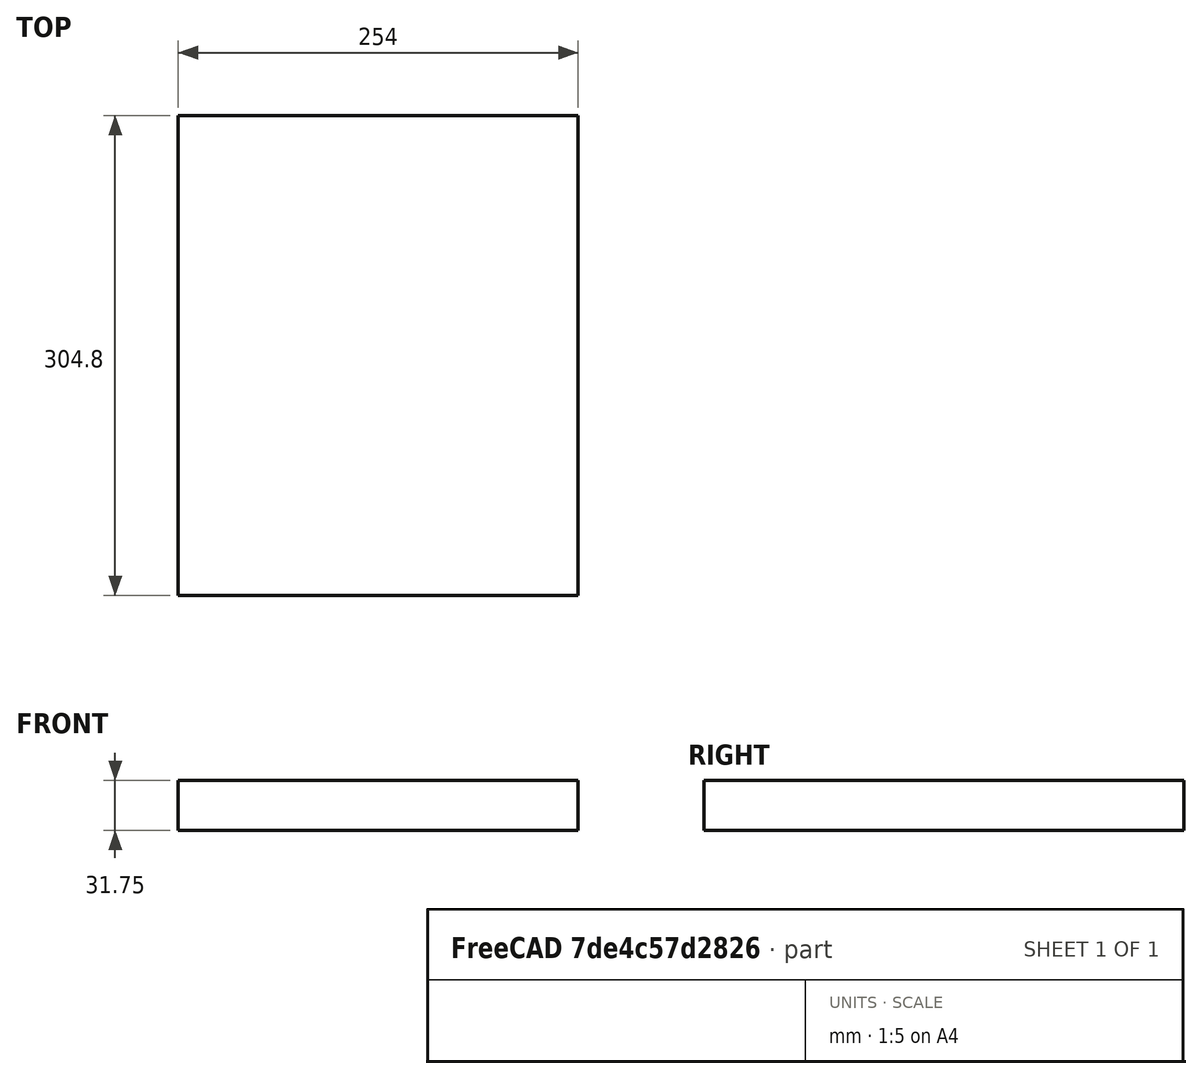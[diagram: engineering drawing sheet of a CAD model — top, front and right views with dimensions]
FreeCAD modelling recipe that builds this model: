
FCSTD DOCUMENT  (FreeCAD 0.16RUnknown)
Label: Base
License: All rights reserved
LicenseURL: http://en.wikipedia.org/wiki/All_rights_reserved
objects: Sketcher::SketchObject×1, Part::Box×1
note: 2 computed .brp shape members not serialized (recipe doc carries the construction recipe); baked Part::Feature solids carry a one-line shape summary decoded from their .brp

FEATURE [Sketcher::SketchObject] Sketch
  sketch-geometry (4):
    g0: LineSegment StartX=0 StartY=0 StartZ=0 EndX=304.8 EndY=0 EndZ=0
    g1: LineSegment StartX=304.8 StartY=0 StartZ=0 EndX=304.8 EndY=254 EndZ=0
    g2: LineSegment StartX=304.8 StartY=254 StartZ=0 EndX=0 EndY=254 EndZ=0
    g3: LineSegment StartX=0 StartY=254 StartZ=0 EndX=0 EndY=0 EndZ=0
  constraints (11):
    c: Coincident(g0,g1)
    c: Coincident(g1,g2)
    c: Coincident(g2,g3)
    c: Coincident(g3,g0)
    c: Horizontal(g0)
    c: Horizontal(g2)
    c: Vertical(g1)
    c: Vertical(g3)
    c: Coincident(g0,g-1)
    c: DistanceX(g0,g0) = 304.8
    c: DistanceY(g3,g3) = 254
FEATURE [Part::Box] Box  label="Cube"
  Height = 31.75
  Length = 254
  Width = 304.8
